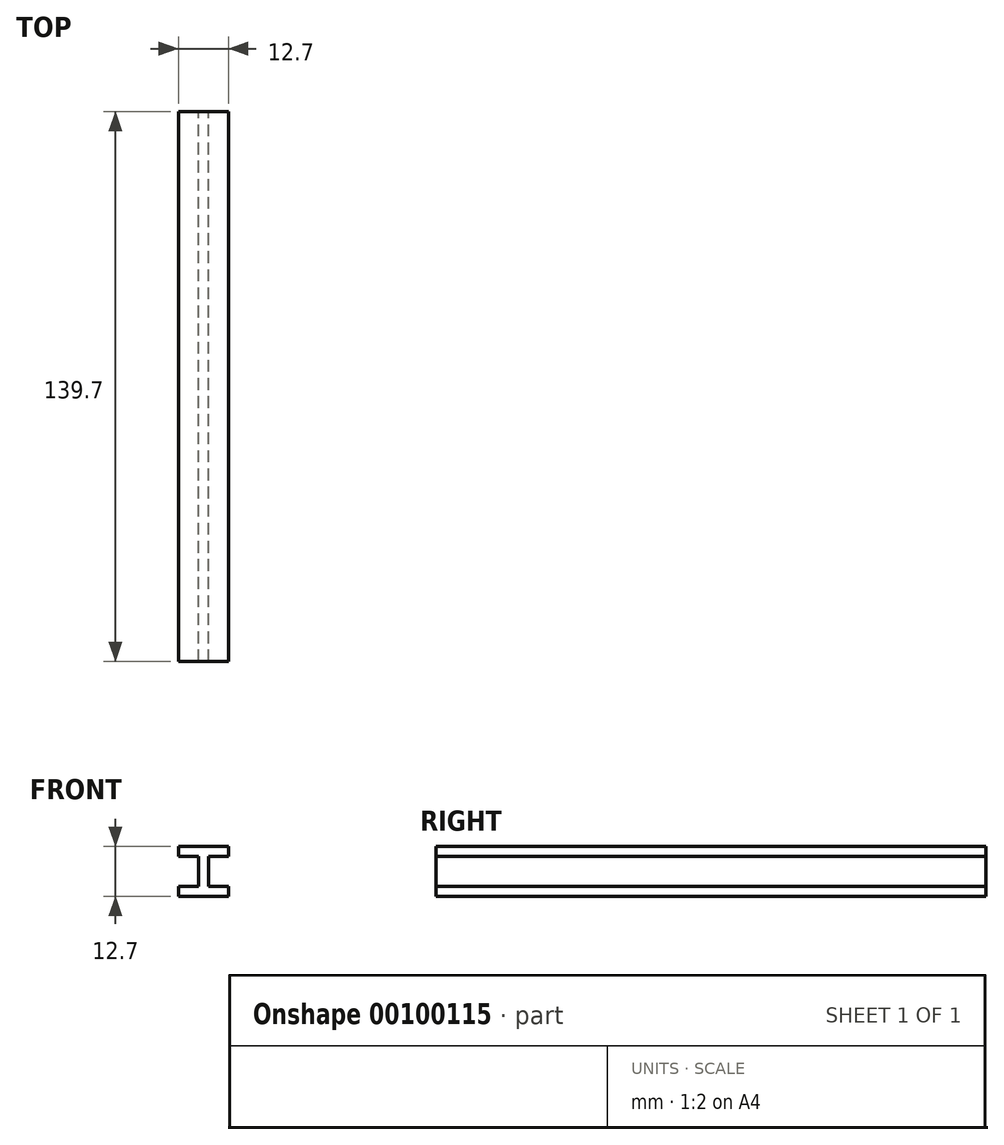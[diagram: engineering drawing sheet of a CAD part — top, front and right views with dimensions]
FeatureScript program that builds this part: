
annotation { "Feature Type Name" : "Feature", "Feature Type Description" : "" }
export const myFeature = defineFeature(function(context is Context, id is Id, definition is map)
    precondition{}
    {
        {
            var Q0;
            Q0=qCreatedBy(makeId("Front.planeOp"),FACE);
            var sketch = newSketch(context, id + "F0", { "sketchPlane" : qUnion([Q0])});
            skLineSegment(sketch, "E0.bottom", {"start": v(1.27, -5.08) * mm, "end": v(-1.27, -5.08) * mm});
            skLineSegment(sketch, "E0.top", {"start": v(1.27, 5.08) * mm, "end": v(-1.27, 5.08) * mm});
            skLineSegment(sketch, "E0.left", {"start": v(1.27, -5.08) * mm, "end": v(1.27, 5.08) * mm});
            skLineSegment(sketch, "E0.right", {"start": v(-1.27, -5.08) * mm, "end": v(-1.27, 5.08) * mm});
            skPoint(sketch, "E0.middle", {"position": v(0, 0) * mm});
            skLineSegment(sketch, "E1.bottom", {"start": v(6.35, -6.35) * mm, "end": v(-6.35, -6.35) * mm});
            skLineSegment(sketch, "E1.top", {"start": v(6.35, -3.8) * mm, "end": v(-6.35, -3.81) * mm});
            skLineSegment(sketch, "E1.left", {"start": v(6.35, -6.35) * mm, "end": v(6.35, -3.81) * mm});
            skLineSegment(sketch, "E1.right", {"start": v(-6.35, -6.35) * mm, "end": v(-6.35, -3.81) * mm});
            skPoint(sketch, "E1.middle", {"position": v(0, -5.08) * mm});
            skLineSegment(sketch, "E2.bottom", {"start": v(6.35, 3.81) * mm, "end": v(-6.35, 3.8) * mm});
            skLineSegment(sketch, "E2.top", {"start": v(6.35, 6.35) * mm, "end": v(-6.35, 6.35) * mm});
            skLineSegment(sketch, "E2.left", {"start": v(6.35, 3.81) * mm, "end": v(6.35, 6.35) * mm});
            skLineSegment(sketch, "E2.right", {"start": v(-6.35, 3.8) * mm, "end": v(-6.35, 6.35) * mm});
            skPoint(sketch, "E2.middle", {"position": v(0, 5.08) * mm});
            skSolve(sketch);
        }
        {
            var Q0;
            {var subQ1=sQuery(id+"F0.wireOp",EDGE,"E0.bottom");Q0=makeQuery(id+"F0.imprint","IMPRINT",FACE,{"disambiguationData":[TD([[makeQuery(id+"F0.imprint","IMPRINT",EDGE,{"derivedFrom":subQ1}),1.0]])]});}
            var Q1;
            {var subQ0=sQuery(id+"F0.wireOp",EDGE,"E0.bottom");Q1=makeQuery(id+"F0.imprint","IMPRINT",FACE,{"disambiguationData":[TD([[makeQuery(id+"F0.imprint","IMPRINT",EDGE,{"derivedFrom":subQ0}),-1.0]])]});}
            var Q2;
            {var subQ0=sQuery(id+"F0.wireOp",EDGE,"E0.top");Q2=makeQuery(id+"F0.imprint","IMPRINT",FACE,{"disambiguationData":[TD([[makeQuery(id+"F0.imprint","IMPRINT",EDGE,{"derivedFrom":subQ0}),1.0]])]});}
            var Q3;
            {var subQ0=sQuery(id+"F0.wireOp",EDGE,"E1.top");var subQ1=sQuery(id+"F0.wireOp",EDGE,"E0.left");var subQ2=makeQuery(id+"F0.imprint","INTERSECT",VERTEX,{"derivedFrom":[subQ1,subQ0]});Q3=makeQuery(id+"F0.imprint","IMPRINT",FACE,{"disambiguationData":[TD([[makeQuery(id+"F0.imprint","IMPRINT",EDGE,{"disambiguationData":[TD([[subQ2,-1.0]])],"derivedFrom":subQ1}),1.0]])]});}
            var Q4;
            {var subQ5=sQuery(id+"F0.wireOp",EDGE,"E0.top");Q4=makeQuery(id+"F0.imprint","IMPRINT",FACE,{"disambiguationData":[TD([[makeQuery(id+"F0.imprint","IMPRINT",EDGE,{"derivedFrom":subQ5}),-1.0]])]});}
            extrude(context, id + "F1", {"entities" : qUnion([Q0, Q1, Q2, Q3, Q4]), "depth" : 139.7 * mm, "symmetric" : true});
        }
    });
